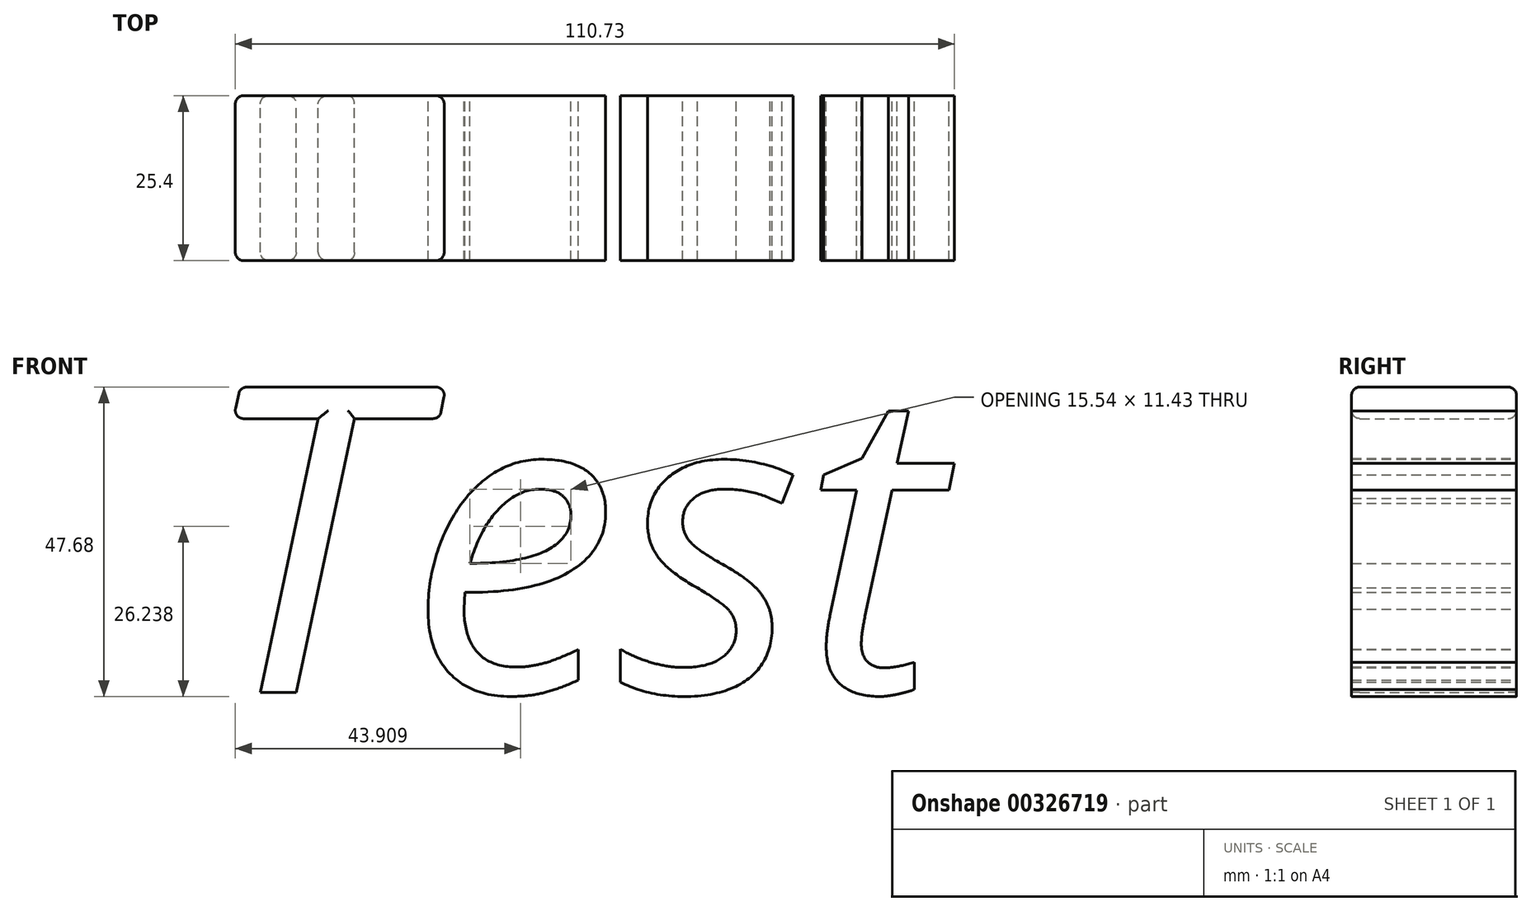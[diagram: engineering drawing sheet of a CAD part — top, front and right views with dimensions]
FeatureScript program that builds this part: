
annotation { "Feature Type Name" : "Feature", "Feature Type Description" : "" }
export const myFeature = defineFeature(function(context is Context, id is Id, definition is map)
    precondition{}
    {
        {
            var Q0;
            Q0=qCreatedBy(makeId("Front.planeOp"),FACE);
            var sketch = newSketch(context, id + "F0", { "sketchPlane" : qUnion([Q0])});
            skLineSegment(sketch, "E0.bottom", {"start": v(0, 0) * mm, "end": v(0, 0) * mm});
            skLineSegment(sketch, "E0.top", {"start": v(0, 0) * mm, "end": v(0, 0) * mm});
            skLineSegment(sketch, "E0.left", {"start": v(0, 0) * mm, "end": v(0, 0) * mm});
            skLineSegment(sketch, "E0.right", {"start": v(0, 0) * mm, "end": v(0, 0) * mm});
            skLineSegment(sketch, "E1.bottom", {"start": v(0, 79.45) * mm, "end": v(80.09, 79.45) * mm});
            skLineSegment(sketch, "E1.top", {"start": v(0, 0) * mm, "end": v(80.09, 0) * mm});
            skLineSegment(sketch, "E1.left", {"start": v(0, 79.45) * mm, "end": v(0, 0) * mm});
            skLineSegment(sketch, "E1.right", {"start": v(80.09, 79.45) * mm, "end": v(80.09, 0) * mm});
            skSolve(sketch);
        }
        {
            var Q0;
            Q0=qCreatedBy(makeId("Front.planeOp"),FACE);
            var sketch = newSketch(context, id + "F1", { "sketchPlane" : qUnion([Q0])});
            skText(sketch, "E2", { "text": "Test", "fontName": "OpenSans-Italic.ttf"});
            const initialGuessF1  = {"E2": [-0.08312, 0.03638, 1, 0, 0.04743]};
            skSetInitialGuess(sketch, initialGuessF1);
            skSolve(sketch);
        }
        {
            var Q0;
            Q0 = qSketchRegion(id + "F1", true);
            extrude(context, id + "F2", {"entities" : qUnion([Q0]), "depth" : 25.4 * mm});
        }
        {
            var Q0;
            Q0=makeQuery(id+"F2.opExtrude","SWEPT_EDGE",EDGE,{"disambiguationData":[OSD([sQuery(id+"F1.wireOp",EDGE,"E2.sketch_text.stroke-3"),sQuery(id+"F1.wireOp",EDGE,"E2.sketch_text.stroke-4")])]});
            var Q1;
            Q1=makeQuery(id+"F2.opExtrude","CAP_EDGE",EDGE,{"disambiguationData":[OSD([sQuery(id+"F1.wireOp",EDGE,"E2.sketch_text.stroke-4")])],"isStart":false});
            var Q2;
            Q2=makeQuery(id+"F2.opExtrude","CAP_EDGE",EDGE,{"disambiguationData":[OSD([sQuery(id+"F1.wireOp",EDGE,"E2.sketch_text.stroke-3")])],"isStart":false});
            var Q3;
            Q3=makeQuery(id+"F2.opExtrude","SWEPT_EDGE",EDGE,{"disambiguationData":[OSD([sQuery(id+"F1.wireOp",EDGE,"E2.sketch_text.stroke-2"),sQuery(id+"F1.wireOp",EDGE,"E2.sketch_text.stroke-3")])]});
            var Q4;
            Q4=makeQuery(id+"F2.opExtrude","CAP_EDGE",EDGE,{"disambiguationData":[OSD([sQuery(id+"F1.wireOp",EDGE,"E2.sketch_text.stroke-2")])],"isStart":false});
            var Q5;
            Q5=makeQuery(id+"F2.opExtrude","CAP_EDGE",EDGE,{"disambiguationData":[OSD([sQuery(id+"F1.wireOp",EDGE,"E2.sketch_text.stroke-1")])],"isStart":false});
            var Q6;
            Q6=makeQuery(id+"F2.opExtrude","CAP_EDGE",EDGE,{"disambiguationData":[OSD([sQuery(id+"F1.wireOp",EDGE,"E2.sketch_text.stroke-7")])],"isStart":false});
            var Q7;
            Q7=makeQuery(id+"F2.opExtrude","CAP_EDGE",EDGE,{"disambiguationData":[OSD([sQuery(id+"F1.wireOp",EDGE,"E2.sketch_text.stroke-1")])],"isStart":true});
            var Q8;
            Q8=makeQuery(id+"F2.opExtrude","CAP_EDGE",EDGE,{"disambiguationData":[OSD([sQuery(id+"F1.wireOp",EDGE,"E2.sketch_text.stroke-6")])],"isStart":false});
            var Q9;
            Q9=makeQuery(id+"F2.opExtrude","CAP_EDGE",EDGE,{"disambiguationData":[OSD([sQuery(id+"F1.wireOp",EDGE,"E2.sketch_text.stroke-5")])],"isStart":false});
            var Q10;
            Q10=makeQuery(id+"F2.opExtrude","SWEPT_EDGE",EDGE,{"disambiguationData":[OSD([sQuery(id+"F1.wireOp",EDGE,"E2.sketch_text.stroke-4"),sQuery(id+"F1.wireOp",EDGE,"E2.sketch_text.stroke-5")])]});
            var Q11;
            Q11=makeQuery(id+"F2.opExtrude","SWEPT_EDGE",EDGE,{"disambiguationData":[OSD([sQuery(id+"F1.wireOp",EDGE,"E2.sketch_text.stroke-5"),sQuery(id+"F1.wireOp",EDGE,"E2.sketch_text.stroke-6")])]});
            var Q12;
            Q12=makeQuery(id+"F2.opExtrude","CAP_EDGE",EDGE,{"disambiguationData":[OSD([sQuery(id+"F1.wireOp",EDGE,"E2.sketch_text.stroke-5")])],"isStart":true});
            var Q13;
            Q13=makeQuery(id+"F2.opExtrude","CAP_EDGE",EDGE,{"disambiguationData":[OSD([sQuery(id+"F1.wireOp",EDGE,"E2.sketch_text.stroke-4")])],"isStart":true});
            var Q14;
            Q14=makeQuery(id+"F2.opExtrude","CAP_EDGE",EDGE,{"disambiguationData":[OSD([sQuery(id+"F1.wireOp",EDGE,"E2.sketch_text.stroke-6")])],"isStart":true});
            var Q15;
            Q15=makeQuery(id+"F2.opExtrude","CAP_EDGE",EDGE,{"disambiguationData":[OSD([sQuery(id+"F1.wireOp",EDGE,"E2.sketch_text.stroke-7")])],"isStart":true});
            var Q16;
            Q16=makeQuery(id+"F2.opExtrude","CAP_EDGE",EDGE,{"disambiguationData":[OSD([sQuery(id+"F1.wireOp",EDGE,"E2.sketch_text.stroke-2")])],"isStart":true});
            var Q17;
            Q17=makeQuery(id+"F2.opExtrude","CAP_EDGE",EDGE,{"disambiguationData":[OSD([sQuery(id+"F1.wireOp",EDGE,"E2.sketch_text.stroke-3")])],"isStart":true});
            fillet(context, id + "F3", {"entities" : qUnion([Q0, Q1, Q2, Q3, Q4, Q5, Q6, Q7, Q8, Q9, Q10, Q11, Q12, Q13, Q14, Q15, Q16, Q17]), "radius" : 1.27 * mm, "tangentPropagation" : true, "allowEdgeOverflow" : false});
        }
    });
